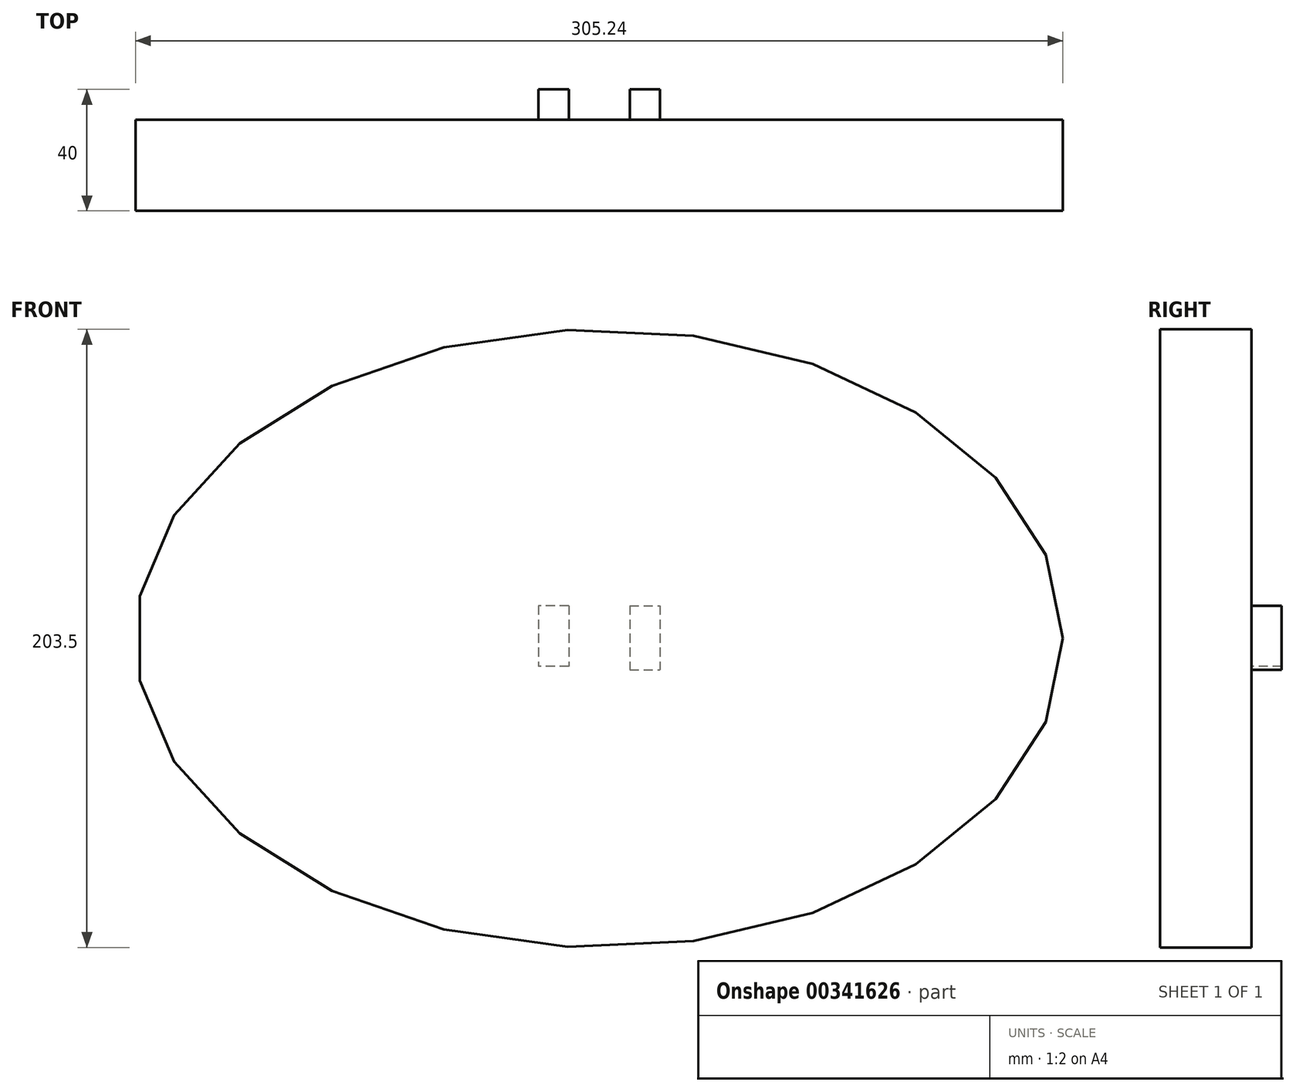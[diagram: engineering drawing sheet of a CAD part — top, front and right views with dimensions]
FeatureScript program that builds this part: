
annotation { "Feature Type Name" : "Feature", "Feature Type Description" : "" }
export const myFeature = defineFeature(function(context is Context, id is Id, definition is map)
    precondition{}
    {
        {
            var Q0;
            Q0=qCreatedBy(makeId("Front.planeOp"),FACE);
            var sketch = newSketch(context, id + "F0", { "sketchPlane" : qUnion([Q0])});
            skEllipse(sketch, "E0", {"center": v(0, 0) * mm, "majorRadius": 152.62 * mm, "minorRadius": 101.75 * mm, "majorAxis": v(1, 0)});
            skLineSegment(sketch, "E1", {"start": v(0, 101.75) * mm, "end": v(0, -101.75) * mm});
            skLineSegment(sketch, "E2", {"start": v(0, -101.75) * mm, "end": v(0, 0) * mm});
            skLineSegment(sketch, "E3", {"start": v(75.37, 0) * mm, "end": v(-74.63, 0) * mm});
            skSolve(sketch);
        }
        {
            var Q0;
            {var subQ0=sQuery(id+"F0.wireOp",EDGE,"E1");Q0=makeQuery(id+"F0.imprint","IMPRINT",FACE,{"disambiguationData":[TD([[makeQuery(id+"F0.imprint","IMPRINT",EDGE,{"derivedFrom":subQ0}),-1.0]])]});}
            var Q1;
            {var subQ0=sQuery(id+"F0.wireOp",EDGE,"E1");Q1=makeQuery(id+"F0.imprint","IMPRINT",FACE,{"disambiguationData":[TD([[makeQuery(id+"F0.imprint","IMPRINT",EDGE,{"derivedFrom":subQ0}),1.0]])]});}
            extrude(context, id + "F1", {"entities" : qUnion([Q0, Q1]), "depth" : 30 * mm});
        }
        {
            var Q0;
            {var subQ0=sQuery(id+"F0.wireOp",EDGE,"E1");Q0=makeQuery(id+"F0.imprint","IMPRINT",FACE,{"disambiguationData":[TD([[makeQuery(id+"F0.imprint","IMPRINT",EDGE,{"derivedFrom":subQ0}),-1.0]])]});}
            var sketch = newSketch(context, id + "F2", { "sketchPlane" : qUnion([Q0])});
            skLineSegment(sketch, "E4.bottom", {"start": v(-10, 10.76) * mm, "end": v(-20, 10.76) * mm});
            skLineSegment(sketch, "E4.top", {"start": v(-10, -9.24) * mm, "end": v(-20, -9.24) * mm});
            skLineSegment(sketch, "E4.left", {"start": v(-10, 10.76) * mm, "end": v(-10, -9.24) * mm});
            skLineSegment(sketch, "E4.right", {"start": v(-20, 10.76) * mm, "end": v(-20, -9.24) * mm});
            skLineSegment(sketch, "E5.bottom", {"start": v(10, 10.76) * mm, "end": v(20, 10.76) * mm});
            skLineSegment(sketch, "E5.top", {"start": v(10, -10.31) * mm, "end": v(20, -10.31) * mm});
            skLineSegment(sketch, "E5.left", {"start": v(10, 10.76) * mm, "end": v(10, -10.31) * mm});
            skLineSegment(sketch, "E5.right", {"start": v(20, 10.76) * mm, "end": v(20, -10.31) * mm});
            skSolve(sketch);
        }
        {
            var Q0;
            Q0 = qSketchRegion(id + "F2", true);
            extrude(context, id + "F3", {"entities" : qUnion([Q0]), "operationType" : NewBodyOperationType.ADD, "oppositeDirection" : true, "depth" : 10 * mm});
        }
    });
